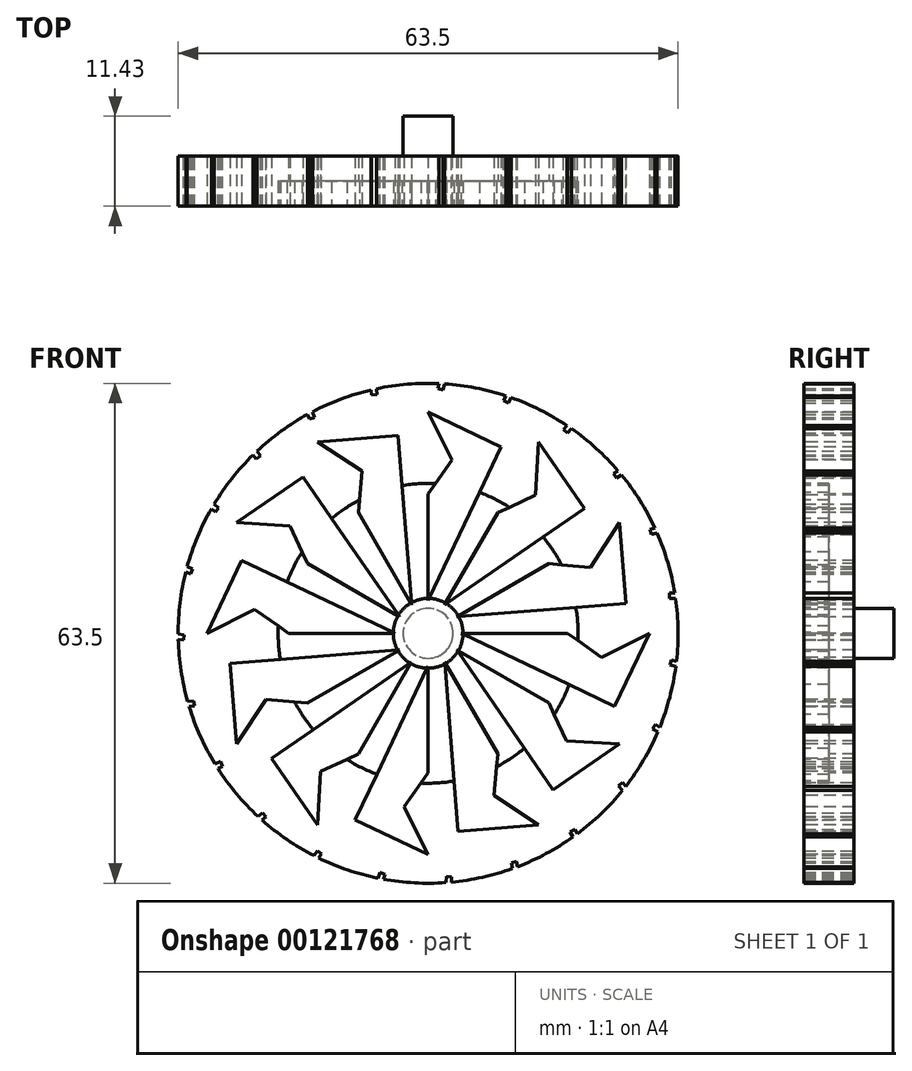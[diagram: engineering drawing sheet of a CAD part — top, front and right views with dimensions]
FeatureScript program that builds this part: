
annotation { "Feature Type Name" : "Feature", "Feature Type Description" : "" }
export const myFeature = defineFeature(function(context is Context, id is Id, definition is map)
    precondition{}
    {
        {
            var Q0;
            Q0=qCreatedBy(makeId("Front.planeOp"),FACE);
            var sketch = newSketch(context, id + "F0", { "sketchPlane" : qUnion([Q0])});
            skCircle(sketch, "E0", {"center": v(0, 0) * mm, "radius": 31.75 * mm});
            skSolve(sketch);
        }
        {
            var Q0;
            Q0 = qSketchRegion(id + "F0", true);
            extrude(context, id + "F1", {"entities" : qUnion([Q0]), "oppositeDirection" : true, "depth" : 6.35 * mm});
        }
        {
            var Q0;
            Q0=makeQuery(id+"F1.opExtrude","CAP_FACE",FACE,{"disambiguationData":[OSD([sQuery(id+"F0.wireOp",EDGE,"E0")])],"isStart":false});
            var sketch = newSketch(context, id + "F2", { "sketchPlane" : qUnion([Q0])});
            skLineSegment(sketch, "E1", {"start": v(-31.34, 5.1) * mm, "end": v(-30.68, 5.1) * mm});
            skLineSegment(sketch, "E2", {"start": v(-30.68, 5.1) * mm, "end": v(-30.68, 4.43) * mm});
            skLineSegment(sketch, "E3", {"start": v(-30.68, 4.43) * mm, "end": v(-31.44, 4.43) * mm});
            skLineSegment(sketch, "E4.1.0", {"start": v(-28.8, 13.36) * mm, "end": v(-28.16, 13.19) * mm});
            skLineSegment(sketch, "E4.1.1", {"start": v(-28.34, 12.54) * mm, "end": v(-29.08, 12.75) * mm});
            skLineSegment(sketch, "E4.1.2", {"start": v(-28.16, 13.19) * mm, "end": v(-28.34, 12.54) * mm});
            skLineSegment(sketch, "E4.2.0", {"start": v(-24.13, 20.64) * mm, "end": v(-23.56, 20.3) * mm});
            skLineSegment(sketch, "E4.2.1", {"start": v(-23.9, 19.72) * mm, "end": v(-24.56, 20.12) * mm});
            skLineSegment(sketch, "E4.2.2", {"start": v(-23.56, 20.3) * mm, "end": v(-23.9, 19.72) * mm});
            skLineSegment(sketch, "E4.3.0", {"start": v(-17.66, 26.38) * mm, "end": v(-17.21, 25.9) * mm});
            skLineSegment(sketch, "E4.3.1", {"start": v(-17.7, 25.44) * mm, "end": v(-18.22, 26) * mm});
            skLineSegment(sketch, "E4.3.2", {"start": v(-17.21, 25.9) * mm, "end": v(-17.7, 25.44) * mm});
            skLineSegment(sketch, "E4.4.0", {"start": v(-9.89, 30.17) * mm, "end": v(-9.59, 29.58) * mm});
            skLineSegment(sketch, "E4.4.1", {"start": v(-10.18, 29.28) * mm, "end": v(-10.53, 29.95) * mm});
            skLineSegment(sketch, "E4.4.2", {"start": v(-9.59, 29.58) * mm, "end": v(-10.18, 29.28) * mm});
            skLineSegment(sketch, "E4.5.0", {"start": v(-1.38, 31.72) * mm, "end": v(-1.25, 31.07) * mm});
            skLineSegment(sketch, "E4.5.1", {"start": v(-1.9, 30.94) * mm, "end": v(-2.06, 31.68) * mm});
            skLineSegment(sketch, "E4.5.2", {"start": v(-1.25, 31.07) * mm, "end": v(-1.9, 30.94) * mm});
            skLineSegment(sketch, "E4.6.0", {"start": v(7.23, 30.92) * mm, "end": v(7.18, 30.26) * mm});
            skLineSegment(sketch, "E4.6.1", {"start": v(6.51, 30.3) * mm, "end": v(6.56, 31.06) * mm});
            skLineSegment(sketch, "E4.6.2", {"start": v(7.18, 30.26) * mm, "end": v(6.51, 30.3) * mm});
            skLineSegment(sketch, "E4.7.0", {"start": v(15.3, 27.82) * mm, "end": v(15.08, 27.2) * mm});
            skLineSegment(sketch, "E4.7.1", {"start": v(14.45, 27.42) * mm, "end": v(14.7, 28.14) * mm});
            skLineSegment(sketch, "E4.7.2", {"start": v(15.08, 27.2) * mm, "end": v(14.45, 27.42) * mm});
            skLineSegment(sketch, "E4.8.0", {"start": v(22.24, 22.66) * mm, "end": v(21.86, 22.12) * mm});
            skLineSegment(sketch, "E4.8.1", {"start": v(21.31, 22.5) * mm, "end": v(21.75, 23.13) * mm});
            skLineSegment(sketch, "E4.8.2", {"start": v(21.86, 22.12) * mm, "end": v(21.31, 22.5) * mm});
            skLineSegment(sketch, "E4.9.0", {"start": v(27.53, 15.82) * mm, "end": v(27.01, 15.4) * mm});
            skLineSegment(sketch, "E4.9.1", {"start": v(26.6, 15.92) * mm, "end": v(27.18, 16.4) * mm});
            skLineSegment(sketch, "E4.9.2", {"start": v(27.01, 15.4) * mm, "end": v(26.6, 15.92) * mm});
            skLineSegment(sketch, "E4.10.0", {"start": v(30.77, 7.8) * mm, "end": v(30.17, 7.54) * mm});
            skLineSegment(sketch, "E4.10.1", {"start": v(29.9, 8.16) * mm, "end": v(30.6, 8.46) * mm});
            skLineSegment(sketch, "E4.10.2", {"start": v(30.17, 7.54) * mm, "end": v(29.9, 8.16) * mm});
            skLineSegment(sketch, "E4.11.0", {"start": v(31.74, -0.78) * mm, "end": v(31.09, -0.87) * mm});
            skLineSegment(sketch, "E4.11.1", {"start": v(31, -0.21) * mm, "end": v(31.75, -0.1) * mm});
            skLineSegment(sketch, "E4.11.2", {"start": v(31.09, -0.87) * mm, "end": v(31, -0.21) * mm});
            skPoint(sketch, "E4.center", {"position": v(0, 0) * mm});
            skLineSegment(sketch, "E4.anchor1", {"start": v(0, 0) * mm, "end": v(-31.34, 5.1) * mm, "construction": true});
            skLineSegment(sketch, "E4.anchor2", {"start": v(0, 0) * mm, "end": v(-31.34, 5.1) * mm, "construction": true});
            skArc(sketch, "E5", {"start": v(-9.89, 30.17) * mm, "mid": v(-10.21, 30.06) * mm, "end": v(-10.53, 29.95) * mm});
            skArc(sketch, "E6.trimOffspring", {"start": v(-17.66, 26.38) * mm, "mid": v(-17.94, 26.2) * mm, "end": v(-18.22, 26) * mm});
            skArc(sketch, "E7.trimOffspring", {"start": v(-24.13, 20.64) * mm, "mid": v(-24.34, 20.38) * mm, "end": v(-24.56, 20.12) * mm});
            skArc(sketch, "E8.trimOffspring", {"start": v(-28.8, 13.36) * mm, "mid": v(-28.94, 13.06) * mm, "end": v(-29.08, 12.75) * mm});
            skArc(sketch, "E9.trimOffspring", {"start": v(-31.34, 5.1) * mm, "mid": v(-31.4, 4.76) * mm, "end": v(-31.44, 4.43) * mm});
            skArc(sketch, "E10.trimOffspring", {"start": v(30.77, 7.8) * mm, "mid": v(30.69, 8.14) * mm, "end": v(30.6, 8.46) * mm});
            skArc(sketch, "E11.trimOffspring", {"start": v(27.53, 15.82) * mm, "mid": v(27.36, 16.11) * mm, "end": v(27.18, 16.4) * mm});
            skArc(sketch, "E12.trimOffspring", {"start": v(22.24, 22.66) * mm, "mid": v(22, 22.9) * mm, "end": v(21.75, 23.13) * mm});
            skArc(sketch, "E13.trimOffspring", {"start": v(15.3, 27.82) * mm, "mid": v(15, 27.98) * mm, "end": v(14.7, 28.14) * mm});
            skArc(sketch, "E14.trimOffspring", {"start": v(7.23, 30.92) * mm, "mid": v(6.9, 31) * mm, "end": v(6.56, 31.06) * mm});
            skArc(sketch, "E15.trimOffspring", {"start": v(-1.38, 31.72) * mm, "mid": v(-1.72, 31.7) * mm, "end": v(-2.06, 31.68) * mm});
            skLineSegment(sketch, "E16.1.12.0", {"start": v(30.35, -9.32) * mm, "end": v(29.7, -9.23) * mm});
            skLineSegment(sketch, "E16.3.12.0", {"start": v(29.79, -8.57) * mm, "end": v(30.54, -8.67) * mm});
            skLineSegment(sketch, "E16.6.12.0", {"start": v(29.7, -9.23) * mm, "end": v(29.79, -8.57) * mm});
            skLineSegment(sketch, "E16.1.13.0", {"start": v(26.71, -17.16) * mm, "end": v(26.1, -16.9) * mm});
            skLineSegment(sketch, "E16.3.13.0", {"start": v(26.37, -16.29) * mm, "end": v(27.07, -16.59) * mm});
            skLineSegment(sketch, "E16.6.13.0", {"start": v(26.1, -16.9) * mm, "end": v(26.37, -16.29) * mm});
            skLineSegment(sketch, "E16.1.14.0", {"start": v(21.1, -23.73) * mm, "end": v(20.58, -23.32) * mm});
            skLineSegment(sketch, "E16.3.14.0", {"start": v(21, -22.8) * mm, "end": v(21.6, -23.28) * mm});
            skLineSegment(sketch, "E16.6.14.0", {"start": v(20.58, -23.32) * mm, "end": v(21, -22.8) * mm});
            skLineSegment(sketch, "E16.1.15.0", {"start": v(13.9, -28.54) * mm, "end": v(13.53, -28) * mm});
            skLineSegment(sketch, "E16.3.15.0", {"start": v(14.07, -27.62) * mm, "end": v(14.51, -28.24) * mm});
            skLineSegment(sketch, "E16.6.15.0", {"start": v(13.53, -28) * mm, "end": v(14.07, -27.62) * mm});
            skLineSegment(sketch, "E16.1.16.0", {"start": v(5.69, -31.24) * mm, "end": v(5.47, -30.61) * mm});
            skLineSegment(sketch, "E16.3.16.0", {"start": v(6.1, -30.39) * mm, "end": v(6.35, -31.1) * mm});
            skLineSegment(sketch, "E16.6.16.0", {"start": v(5.47, -30.61) * mm, "end": v(6.1, -30.39) * mm});
            skLineSegment(sketch, "E16.1.17.0", {"start": v(-2.95, -31.61) * mm, "end": v(-3, -30.95) * mm});
            skLineSegment(sketch, "E16.3.17.0", {"start": v(-2.33, -30.9) * mm, "end": v(-2.27, -31.67) * mm});
            skLineSegment(sketch, "E16.6.17.0", {"start": v(-3, -30.95) * mm, "end": v(-2.33, -30.9) * mm});
            skLineSegment(sketch, "E16.1.18.0", {"start": v(-11.37, -29.64) * mm, "end": v(-11.23, -29) * mm});
            skLineSegment(sketch, "E16.3.18.0", {"start": v(-10.58, -29.13) * mm, "end": v(-10.73, -29.88) * mm});
            skLineSegment(sketch, "E16.6.18.0", {"start": v(-11.23, -29) * mm, "end": v(-10.58, -29.13) * mm});
            skLineSegment(sketch, "E16.1.19.0", {"start": v(-18.94, -25.48) * mm, "end": v(-18.64, -24.9) * mm});
            skLineSegment(sketch, "E16.3.19.0", {"start": v(-18.05, -25.2) * mm, "end": v(-18.4, -25.88) * mm});
            skLineSegment(sketch, "E16.6.19.0", {"start": v(-18.64, -24.9) * mm, "end": v(-18.05, -25.2) * mm});
            skLineSegment(sketch, "E16.1.20.0", {"start": v(-25.12, -19.42) * mm, "end": v(-24.67, -18.94) * mm});
            skLineSegment(sketch, "E16.3.20.0", {"start": v(-24.18, -19.4) * mm, "end": v(-24.7, -19.95) * mm});
            skLineSegment(sketch, "E16.6.20.0", {"start": v(-24.67, -18.94) * mm, "end": v(-24.18, -19.4) * mm});
            skLineSegment(sketch, "E16.1.21.0", {"start": v(-29.43, -11.93) * mm, "end": v(-28.86, -11.58) * mm});
            skLineSegment(sketch, "E16.3.21.0", {"start": v(-28.51, -12.15) * mm, "end": v(-29.16, -12.55) * mm});
            skLineSegment(sketch, "E16.6.21.0", {"start": v(-28.86, -11.58) * mm, "end": v(-28.51, -12.15) * mm});
            skLineSegment(sketch, "E16.1.22.0", {"start": v(-31.55, -3.54) * mm, "end": v(-30.92, -3.37) * mm});
            skLineSegment(sketch, "E16.3.22.0", {"start": v(-30.73, -4.01) * mm, "end": v(-31.47, -4.22) * mm});
            skLineSegment(sketch, "E16.6.22.0", {"start": v(-30.92, -3.37) * mm, "end": v(-30.73, -4.01) * mm});
            skSolve(sketch);
        }
        {
            var Q0;
            Q0 = qSketchRegion(id + "F2", true);
            var Q1;
            {var subQ0=sQuery(id+"F2.wireOp",EDGE,"E16.1.12.0");Q1=makeQuery(id+"F2.imprint","IMPRINT",FACE,{"disambiguationData":[TD([[makeQuery(id+"F2.imprint","IMPRINT",EDGE,{"derivedFrom":subQ0}),-1.0]])]});}
            var Q2;
            {var subQ0=sQuery(id+"F2.wireOp",EDGE,"E4.11.0");Q2=makeQuery(id+"F2.imprint","IMPRINT",FACE,{"disambiguationData":[TD([[makeQuery(id+"F2.imprint","IMPRINT",EDGE,{"derivedFrom":subQ0}),-1.0]])]});}
            var Q3;
            {var subQ0=sQuery(id+"F2.wireOp",EDGE,"E16.1.13.0");Q3=makeQuery(id+"F2.imprint","IMPRINT",FACE,{"disambiguationData":[TD([[makeQuery(id+"F2.imprint","IMPRINT",EDGE,{"derivedFrom":subQ0}),-1.0]])]});}
            var Q4;
            {var subQ0=sQuery(id+"F2.wireOp",EDGE,"E16.1.14.0");Q4=makeQuery(id+"F2.imprint","IMPRINT",FACE,{"disambiguationData":[TD([[makeQuery(id+"F2.imprint","IMPRINT",EDGE,{"derivedFrom":subQ0}),-1.0]])]});}
            var Q5;
            {var subQ0=sQuery(id+"F2.wireOp",EDGE,"E16.1.15.0");Q5=makeQuery(id+"F2.imprint","IMPRINT",FACE,{"disambiguationData":[TD([[makeQuery(id+"F2.imprint","IMPRINT",EDGE,{"derivedFrom":subQ0}),-1.0]])]});}
            var Q6;
            {var subQ0=sQuery(id+"F2.wireOp",EDGE,"E16.1.16.0");Q6=makeQuery(id+"F2.imprint","IMPRINT",FACE,{"disambiguationData":[TD([[makeQuery(id+"F2.imprint","IMPRINT",EDGE,{"derivedFrom":subQ0}),-1.0]])]});}
            var Q7;
            {var subQ0=sQuery(id+"F2.wireOp",EDGE,"E16.1.17.0");Q7=makeQuery(id+"F2.imprint","IMPRINT",FACE,{"disambiguationData":[TD([[makeQuery(id+"F2.imprint","IMPRINT",EDGE,{"derivedFrom":subQ0}),-1.0]])]});}
            var Q8;
            {var subQ0=sQuery(id+"F2.wireOp",EDGE,"E16.1.18.0");Q8=makeQuery(id+"F2.imprint","IMPRINT",FACE,{"disambiguationData":[TD([[makeQuery(id+"F2.imprint","IMPRINT",EDGE,{"derivedFrom":subQ0}),-1.0]])]});}
            var Q9;
            {var subQ0=sQuery(id+"F2.wireOp",EDGE,"E16.1.19.0");Q9=makeQuery(id+"F2.imprint","IMPRINT",FACE,{"disambiguationData":[TD([[makeQuery(id+"F2.imprint","IMPRINT",EDGE,{"derivedFrom":subQ0}),-1.0]])]});}
            var Q10;
            {var subQ0=sQuery(id+"F2.wireOp",EDGE,"E16.1.20.0");Q10=makeQuery(id+"F2.imprint","IMPRINT",FACE,{"disambiguationData":[TD([[makeQuery(id+"F2.imprint","IMPRINT",EDGE,{"derivedFrom":subQ0}),-1.0]])]});}
            var Q11;
            {var subQ0=sQuery(id+"F2.wireOp",EDGE,"E16.1.21.0");Q11=makeQuery(id+"F2.imprint","IMPRINT",FACE,{"disambiguationData":[TD([[makeQuery(id+"F2.imprint","IMPRINT",EDGE,{"derivedFrom":subQ0}),-1.0]])]});}
            var Q12;
            {var subQ0=sQuery(id+"F2.wireOp",EDGE,"E16.1.22.0");Q12=makeQuery(id+"F2.imprint","IMPRINT",FACE,{"disambiguationData":[TD([[makeQuery(id+"F2.imprint","IMPRINT",EDGE,{"derivedFrom":subQ0}),-1.0]])]});}
            var Q13;
            Q13=makeQuery(id+"F1.opExtrude","CAP_FACE",FACE,{"disambiguationData":[OSD([sQuery(id+"F0.wireOp",EDGE,"E0")])],"isStart":true});
            extrude(context, id + "F3", {"entities" : qUnion([Q0, Q1, Q2, Q3, Q4, Q5, Q6, Q7, Q8, Q9, Q10, Q11, Q12]), "operationType" : NewBodyOperationType.REMOVE, "endBound" : BoundingType.UP_TO_SURFACE, "oppositeDirection" : true, "endBoundEntityFace" : qUnion([Q13]), "depth" : 25.4 * mm});
        }
        {
            var Q0;
            Q0=makeQuery(id+"F1.opExtrude","CAP_FACE",FACE,{"disambiguationData":[OSD([sQuery(id+"F0.wireOp",EDGE,"E0")])],"isStart":true});
            var sketch = newSketch(context, id + "F4", { "sketchPlane" : qUnion([Q0])});
            skLineSegment(sketch, "E17", {"start": v(-28.1, 0) * mm, "end": v(-23.7, 9.27) * mm});
            skLineSegment(sketch, "E18", {"start": v(-23.7, 9.27) * mm, "end": v(-4.2, 0) * mm});
            skLineSegment(sketch, "E19", {"start": v(-4.2, 0) * mm, "end": v(-17.7, 0) * mm});
            skLineSegment(sketch, "E20", {"start": v(-17.7, 0) * mm, "end": v(-22.03, 3.04) * mm});
            skLineSegment(sketch, "E21", {"start": v(-22.03, 3.04) * mm, "end": v(-28.1, 0) * mm});
            skLineSegment(sketch, "E22.1.0", {"start": v(-15.33, -8.85) * mm, "end": v(-20.6, -8.39) * mm});
            skLineSegment(sketch, "E22.1.1", {"start": v(-20.6, -8.39) * mm, "end": v(-24.33, -14.05) * mm});
            skLineSegment(sketch, "E22.1.2", {"start": v(-24.33, -14.05) * mm, "end": v(-25.15, -3.82) * mm});
            skLineSegment(sketch, "E22.1.3", {"start": v(-25.15, -3.82) * mm, "end": v(-3.63, -2.1) * mm});
            skLineSegment(sketch, "E22.1.4", {"start": v(-3.63, -2.1) * mm, "end": v(-15.33, -8.85) * mm});
            skLineSegment(sketch, "E22.2.0", {"start": v(-8.85, -15.33) * mm, "end": v(-13.65, -17.56) * mm});
            skLineSegment(sketch, "E22.2.1", {"start": v(-13.65, -17.56) * mm, "end": v(-14.05, -24.33) * mm});
            skLineSegment(sketch, "E22.2.2", {"start": v(-14.05, -24.33) * mm, "end": v(-19.87, -15.88) * mm});
            skLineSegment(sketch, "E22.2.3", {"start": v(-19.87, -15.88) * mm, "end": v(-2.1, -3.63) * mm});
            skLineSegment(sketch, "E22.2.4", {"start": v(-2.1, -3.63) * mm, "end": v(-8.85, -15.33) * mm});
            skLineSegment(sketch, "E22.3.0", {"start": v(0, -17.7) * mm, "end": v(-3.04, -22.03) * mm});
            skLineSegment(sketch, "E22.3.1", {"start": v(-3.04, -22.03) * mm, "end": v(0, -28.1) * mm});
            skLineSegment(sketch, "E22.3.2", {"start": v(0, -28.1) * mm, "end": v(-9.27, -23.7) * mm});
            skLineSegment(sketch, "E22.3.3", {"start": v(-9.27, -23.7) * mm, "end": v(0, -4.2) * mm});
            skLineSegment(sketch, "E22.3.4", {"start": v(0, -4.2) * mm, "end": v(0, -17.7) * mm});
            skLineSegment(sketch, "E22.4.0", {"start": v(8.85, -15.33) * mm, "end": v(8.39, -20.6) * mm});
            skLineSegment(sketch, "E22.4.1", {"start": v(8.39, -20.6) * mm, "end": v(14.05, -24.33) * mm});
            skLineSegment(sketch, "E22.4.2", {"start": v(14.05, -24.33) * mm, "end": v(3.82, -25.15) * mm});
            skLineSegment(sketch, "E22.4.3", {"start": v(3.82, -25.15) * mm, "end": v(2.1, -3.63) * mm});
            skLineSegment(sketch, "E22.4.4", {"start": v(2.1, -3.63) * mm, "end": v(8.85, -15.33) * mm});
            skLineSegment(sketch, "E22.5.0", {"start": v(15.33, -8.85) * mm, "end": v(17.56, -13.65) * mm});
            skLineSegment(sketch, "E22.5.1", {"start": v(17.56, -13.65) * mm, "end": v(24.33, -14.05) * mm});
            skLineSegment(sketch, "E22.5.2", {"start": v(24.33, -14.05) * mm, "end": v(15.88, -19.87) * mm});
            skLineSegment(sketch, "E22.5.3", {"start": v(15.88, -19.87) * mm, "end": v(3.63, -2.1) * mm});
            skLineSegment(sketch, "E22.5.4", {"start": v(3.63, -2.1) * mm, "end": v(15.33, -8.85) * mm});
            skLineSegment(sketch, "E22.6.0", {"start": v(17.7, 0) * mm, "end": v(22.03, -3.04) * mm});
            skLineSegment(sketch, "E22.6.1", {"start": v(22.03, -3.04) * mm, "end": v(28.1, 0) * mm});
            skLineSegment(sketch, "E22.6.2", {"start": v(28.1, 0) * mm, "end": v(23.7, -9.27) * mm});
            skLineSegment(sketch, "E22.6.3", {"start": v(23.7, -9.27) * mm, "end": v(4.2, 0) * mm});
            skLineSegment(sketch, "E22.6.4", {"start": v(4.2, 0) * mm, "end": v(17.7, 0) * mm});
            skLineSegment(sketch, "E22.7.0", {"start": v(15.33, 8.85) * mm, "end": v(20.6, 8.39) * mm});
            skLineSegment(sketch, "E22.7.1", {"start": v(20.6, 8.39) * mm, "end": v(24.33, 14.05) * mm});
            skLineSegment(sketch, "E22.7.2", {"start": v(24.33, 14.05) * mm, "end": v(25.15, 3.82) * mm});
            skLineSegment(sketch, "E22.7.3", {"start": v(25.15, 3.82) * mm, "end": v(3.63, 2.1) * mm});
            skLineSegment(sketch, "E22.7.4", {"start": v(3.63, 2.1) * mm, "end": v(15.33, 8.85) * mm});
            skLineSegment(sketch, "E22.8.0", {"start": v(8.85, 15.33) * mm, "end": v(13.65, 17.56) * mm});
            skLineSegment(sketch, "E22.8.1", {"start": v(13.65, 17.56) * mm, "end": v(14.05, 24.33) * mm});
            skLineSegment(sketch, "E22.8.2", {"start": v(14.05, 24.33) * mm, "end": v(19.87, 15.88) * mm});
            skLineSegment(sketch, "E22.8.3", {"start": v(19.87, 15.88) * mm, "end": v(2.1, 3.63) * mm});
            skLineSegment(sketch, "E22.8.4", {"start": v(2.1, 3.63) * mm, "end": v(8.85, 15.33) * mm});
            skLineSegment(sketch, "E22.9.0", {"start": v(0, 17.7) * mm, "end": v(3.04, 22.03) * mm});
            skLineSegment(sketch, "E22.9.1", {"start": v(3.04, 22.03) * mm, "end": v(0, 28.1) * mm});
            skLineSegment(sketch, "E22.9.2", {"start": v(0, 28.1) * mm, "end": v(9.27, 23.7) * mm});
            skLineSegment(sketch, "E22.9.3", {"start": v(9.27, 23.7) * mm, "end": v(0, 4.2) * mm});
            skLineSegment(sketch, "E22.9.4", {"start": v(0, 4.2) * mm, "end": v(0, 17.7) * mm});
            skLineSegment(sketch, "E22.10.0", {"start": v(-8.85, 15.33) * mm, "end": v(-8.39, 20.6) * mm});
            skLineSegment(sketch, "E22.10.1", {"start": v(-8.39, 20.6) * mm, "end": v(-14.05, 24.33) * mm});
            skLineSegment(sketch, "E22.10.2", {"start": v(-14.05, 24.33) * mm, "end": v(-3.82, 25.15) * mm});
            skLineSegment(sketch, "E22.10.3", {"start": v(-3.82, 25.15) * mm, "end": v(-2.1, 3.63) * mm});
            skLineSegment(sketch, "E22.10.4", {"start": v(-2.1, 3.63) * mm, "end": v(-8.85, 15.33) * mm});
            skLineSegment(sketch, "E22.11.0", {"start": v(-15.33, 8.85) * mm, "end": v(-17.56, 13.65) * mm});
            skLineSegment(sketch, "E22.11.1", {"start": v(-17.56, 13.65) * mm, "end": v(-24.33, 14.05) * mm});
            skLineSegment(sketch, "E22.11.2", {"start": v(-24.33, 14.05) * mm, "end": v(-15.88, 19.87) * mm});
            skLineSegment(sketch, "E22.11.3", {"start": v(-15.88, 19.87) * mm, "end": v(-3.63, 2.1) * mm});
            skLineSegment(sketch, "E22.11.4", {"start": v(-3.63, 2.1) * mm, "end": v(-15.33, 8.85) * mm});
            skPoint(sketch, "E22.center", {"position": v(0, 0) * mm});
            skSolve(sketch);
        }
        {
            var Q0;
            Q0=makeQuery(id+"F4.imprint","IMPRINT",FACE,{"disambiguationData":[TD([[makeQuery(id+"F4.imprint","IMPRINT",EDGE,{"derivedFrom":sQuery(id+"F4.wireOp",EDGE,"E17")}),-1.0]])]});
            var Q1;
            Q1=makeQuery(id+"F4.imprint","IMPRINT",FACE,{"disambiguationData":[TD([[makeQuery(id+"F4.imprint","IMPRINT",EDGE,{"derivedFrom":sQuery(id+"F4.wireOp",EDGE,"E22.11.0")}),-1.0]])]});
            var Q2;
            Q2=makeQuery(id+"F4.imprint","IMPRINT",FACE,{"disambiguationData":[TD([[makeQuery(id+"F4.imprint","IMPRINT",EDGE,{"derivedFrom":sQuery(id+"F4.wireOp",EDGE,"E22.10.0")}),-1.0]])]});
            var Q3;
            Q3=makeQuery(id+"F4.imprint","IMPRINT",FACE,{"disambiguationData":[TD([[makeQuery(id+"F4.imprint","IMPRINT",EDGE,{"derivedFrom":sQuery(id+"F4.wireOp",EDGE,"E22.9.0")}),-1.0]])]});
            var Q4;
            Q4=makeQuery(id+"F4.imprint","IMPRINT",FACE,{"disambiguationData":[TD([[makeQuery(id+"F4.imprint","IMPRINT",EDGE,{"derivedFrom":sQuery(id+"F4.wireOp",EDGE,"E22.8.0")}),-1.0]])]});
            var Q5;
            Q5=makeQuery(id+"F4.imprint","IMPRINT",FACE,{"disambiguationData":[TD([[makeQuery(id+"F4.imprint","IMPRINT",EDGE,{"derivedFrom":sQuery(id+"F4.wireOp",EDGE,"E22.7.0")}),-1.0]])]});
            var Q6;
            Q6=makeQuery(id+"F4.imprint","IMPRINT",FACE,{"disambiguationData":[TD([[makeQuery(id+"F4.imprint","IMPRINT",EDGE,{"derivedFrom":sQuery(id+"F4.wireOp",EDGE,"E22.6.0")}),-1.0]])]});
            var Q7;
            Q7=makeQuery(id+"F4.imprint","IMPRINT",FACE,{"disambiguationData":[TD([[makeQuery(id+"F4.imprint","IMPRINT",EDGE,{"derivedFrom":sQuery(id+"F4.wireOp",EDGE,"E22.5.0")}),-1.0]])]});
            var Q8;
            Q8=makeQuery(id+"F4.imprint","IMPRINT",FACE,{"disambiguationData":[TD([[makeQuery(id+"F4.imprint","IMPRINT",EDGE,{"derivedFrom":sQuery(id+"F4.wireOp",EDGE,"E22.4.0")}),-1.0]])]});
            var Q9;
            Q9=makeQuery(id+"F4.imprint","IMPRINT",FACE,{"disambiguationData":[TD([[makeQuery(id+"F4.imprint","IMPRINT",EDGE,{"derivedFrom":sQuery(id+"F4.wireOp",EDGE,"E22.3.0")}),-1.0]])]});
            var Q10;
            Q10=makeQuery(id+"F4.imprint","IMPRINT",FACE,{"disambiguationData":[TD([[makeQuery(id+"F4.imprint","IMPRINT",EDGE,{"derivedFrom":sQuery(id+"F4.wireOp",EDGE,"E22.2.0")}),-1.0]])]});
            var Q11;
            Q11=makeQuery(id+"F4.imprint","IMPRINT",FACE,{"disambiguationData":[TD([[makeQuery(id+"F4.imprint","IMPRINT",EDGE,{"derivedFrom":sQuery(id+"F4.wireOp",EDGE,"E22.1.0")}),-1.0]])]});
            var Q12;
            Q12=makeQuery(id+"F1.opExtrude","CAP_FACE",FACE,{"disambiguationData":[OSD([sQuery(id+"F0.wireOp",EDGE,"E0")])],"isStart":false});
            extrude(context, id + "F5", {"entities" : qUnion([Q0, Q1, Q2, Q3, Q4, Q5, Q6, Q7, Q8, Q9, Q10, Q11]), "operationType" : NewBodyOperationType.REMOVE, "endBound" : BoundingType.UP_TO_SURFACE, "oppositeDirection" : true, "endBoundEntityFace" : qUnion([Q12]), "depth" : 25.4 * mm});
        }
        {
            var Q0;
            Q0=makeQuery(id+"F1.opExtrude","CAP_FACE",FACE,{"disambiguationData":[OSD([sQuery(id+"F0.wireOp",EDGE,"E0")])],"isStart":true});
            var sketch = newSketch(context, id + "F6", { "sketchPlane" : qUnion([Q0])});
            skCircle(sketch, "E23", {"center": v(0, 0) * mm, "radius": 19.05 * mm});
            skCircle(sketch, "E24", {"center": v(0, 0) * mm, "radius": 4.43 * mm});
            skSolve(sketch);
        }
        {
            var Q0;
            Q0 = qSketchRegion(id + "F6", true);
            extrude(context, id + "F7", {"entities" : qUnion([Q0]), "operationType" : NewBodyOperationType.REMOVE, "oppositeDirection" : true, "depth" : 3.17 * mm});
        }
        {
            var Q0;
            Q0=makeQuery(id+"F1.opExtrude","CAP_FACE",FACE,{"disambiguationData":[OSD([sQuery(id+"F0.wireOp",EDGE,"E0")])],"isStart":false});
            var sketch = newSketch(context, id + "F8", { "sketchPlane" : qUnion([Q0])});
            skCircle(sketch, "E25", {"center": v(0, 0) * mm, "radius": 3.18 * mm});
            skSolve(sketch);
        }
        {
            var Q0;
            Q0 = qSketchRegion(id + "F8", true);
            extrude(context, id + "F9", {"entities" : qUnion([Q0]), "operationType" : NewBodyOperationType.ADD, "depth" : 5.08 * mm});
        }
    });
